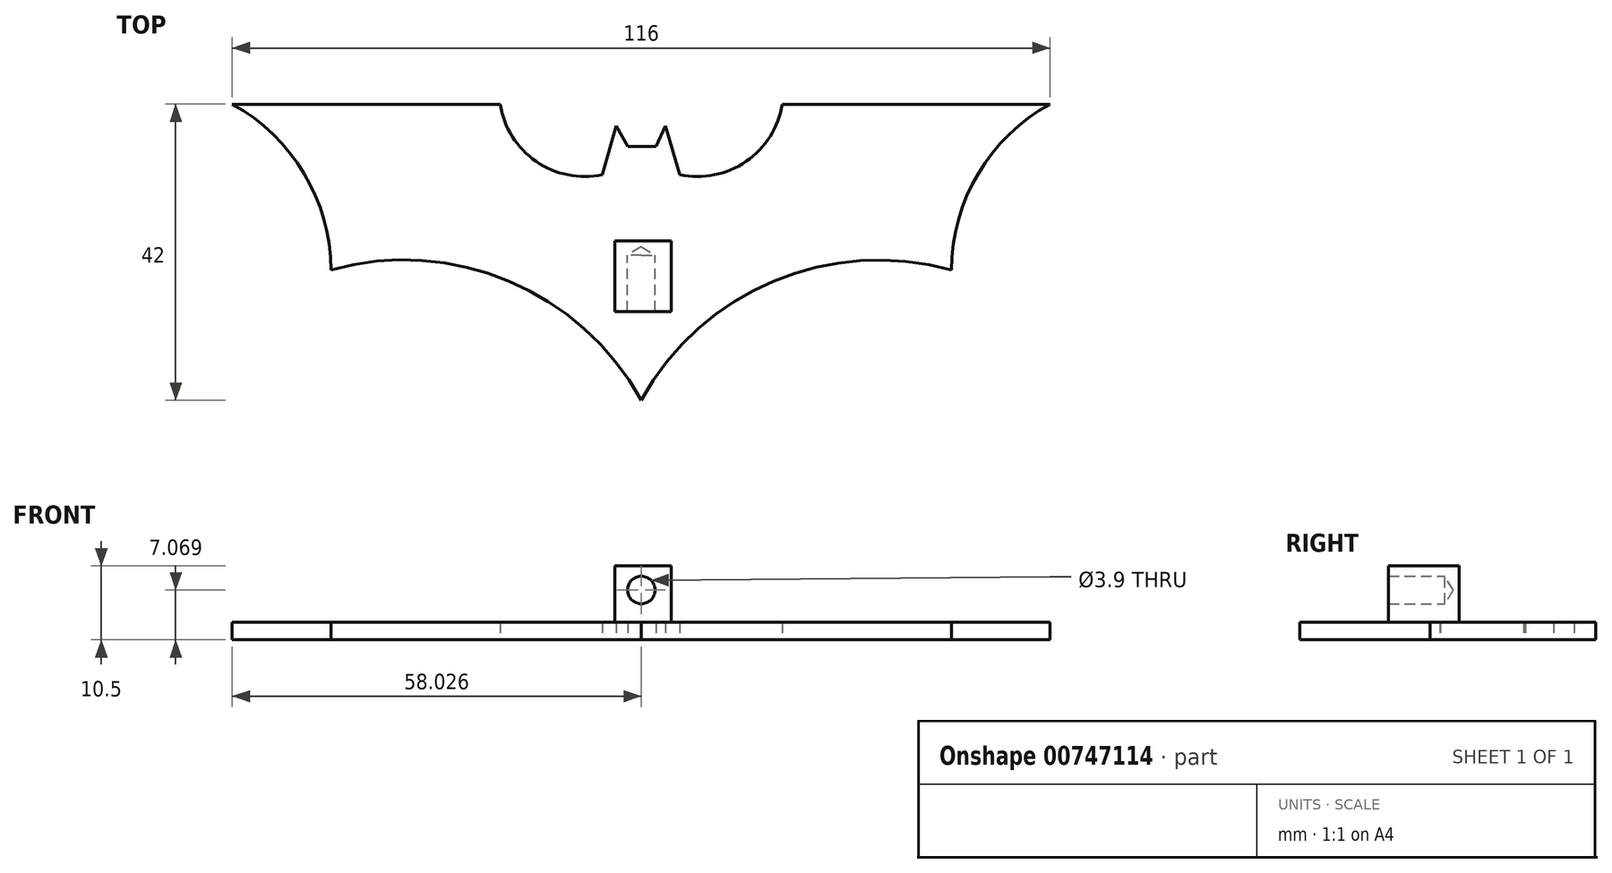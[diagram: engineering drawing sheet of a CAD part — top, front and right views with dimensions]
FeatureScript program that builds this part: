
annotation { "Feature Type Name" : "Feature", "Feature Type Description" : "" }
export const myFeature = defineFeature(function(context is Context, id is Id, definition is map)
    precondition{}
    {
        {
            var Q0;
            Q0=qCreatedBy(makeId("Top.planeOp"),FACE);
            var sketch = newSketch(context, id + "F0", { "sketchPlane" : qUnion([Q0])});
            skLineSegment(sketch, "E0", {"start": v(-58, 14.7) * mm, "end": v(-20, 14.7) * mm});
            skLineSegment(sketch, "E1", {"start": v(20, 14.7) * mm, "end": v(58, 14.7) * mm});
            skLineSegment(sketch, "E2", {"start": v(-5.5, 4.7) * mm, "end": v(-3.54, 11.63) * mm});
            skLineSegment(sketch, "E3", {"start": v(-3.54, 11.63) * mm, "end": v(-1.92, 8.7) * mm});
            skLineSegment(sketch, "E4", {"start": v(-1.92, 8.7) * mm, "end": v(2.08, 8.7) * mm});
            skLineSegment(sketch, "E5", {"start": v(2.08, 8.7) * mm, "end": v(3.46, 11.63) * mm});
            skLineSegment(sketch, "E6", {"start": v(3.46, 11.63) * mm, "end": v(5.5, 4.7) * mm});
            skArc(sketch, "E7", {"start": v(0, -27.3) * mm, "mid": v(-18.78, -10.4) * mm, "end": v(-44, -8.8) * mm});
            skArc(sketch, "E8", {"start": v(44, -8.8) * mm, "mid": v(18.8, -10.43) * mm, "end": v(0, -27.3) * mm});
            skArc(sketch, "E9", {"start": v(5.5, 4.7) * mm, "mid": v(14.9, 6.58) * mm, "end": v(20, 14.7) * mm});
            skArc(sketch, "E10", {"start": v(-20, 14.7) * mm, "mid": v(-14.9, 6.58) * mm, "end": v(-5.5, 4.7) * mm});
            skArc(sketch, "E11", {"start": v(58, 14.7) * mm, "mid": v(47.8, 4.85) * mm, "end": v(44, -8.8) * mm});
            skArc(sketch, "E12", {"start": v(-44, -8.8) * mm, "mid": v(-47.8, 4.85) * mm, "end": v(-58, 14.7) * mm});
            skSolve(sketch);
        }
        {
            var Q0;
            Q0=makeQuery(id+"F0.imprint","IMPRINT",FACE,{"disambiguationData":[TD([[makeQuery(id+"F0.imprint","IMPRINT",EDGE,{"derivedFrom":sQuery(id+"F0.wireOp",EDGE,"E0")}),-1.0]])]});
            extrude(context, id + "F1", {"entities" : qUnion([Q0]), "flatOperationType" : FlatOperationType.REMOVE, "depth" : 2.5 * mm, "offsetDistance" : 25 * mm, "domain" : OperationDomain.MODEL});
        }
        {
            var Q0;
            Q0=makeQuery(id+"F1.opExtrude","CAP_FACE",FACE,{"disambiguationData":[OSD([sQuery(id+"F0.wireOp",EDGE,"E0"),sQuery(id+"F0.wireOp",EDGE,"E1"),sQuery(id+"F0.wireOp",EDGE,"E2"),sQuery(id+"F0.wireOp",EDGE,"E3"),sQuery(id+"F0.wireOp",EDGE,"E4"),sQuery(id+"F0.wireOp",EDGE,"E5"),sQuery(id+"F0.wireOp",EDGE,"E6"),sQuery(id+"F0.wireOp",EDGE,"E7"),sQuery(id+"F0.wireOp",EDGE,"E8"),sQuery(id+"F0.wireOp",EDGE,"E9"),sQuery(id+"F0.wireOp",EDGE,"E10"),sQuery(id+"F0.wireOp",EDGE,"E11"),sQuery(id+"F0.wireOp",EDGE,"E12")])],"isStart":false});
            var sketch = newSketch(context, id + "F2", { "sketchPlane" : qUnion([Q0])});
            skLineSegment(sketch, "E13.bottom", {"start": v(-3.73, -4.71) * mm, "end": v(4.27, -4.71) * mm});
            skLineSegment(sketch, "E13.top", {"start": v(-3.73, -14.71) * mm, "end": v(4.27, -14.71) * mm});
            skLineSegment(sketch, "E13.left", {"start": v(-3.73, -4.71) * mm, "end": v(-3.73, -14.71) * mm});
            skLineSegment(sketch, "E13.right", {"start": v(4.27, -4.71) * mm, "end": v(4.27, -14.71) * mm});
            skSolve(sketch);
        }
        {
            var Q0;
            Q0 = qSketchRegion(id + "F2", true);
            extrude(context, id + "F3", {"entities" : qUnion([Q0]), "operationType" : NewBodyOperationType.ADD, "flatOperationType" : FlatOperationType.REMOVE, "depth" : 8 * mm, "offsetDistance" : 25 * mm, "domain" : OperationDomain.MODEL});
        }
        {
            var Q0;
            Q0=makeQuery(id+"F3.opExtrude","SWEPT_FACE",FACE,{"disambiguationData":[OSD([sQuery(id+"F2.wireOp",EDGE,"E13.top")])]});
            var sketch = newSketch(context, id + "F4", { "sketchPlane" : qUnion([Q0])});
            skCircle(sketch, "E14", {"center": v(0.03, 7.07) * mm, "radius": 1.95 * mm});
            skSolve(sketch);
        }
        {
            var Q0;
            Q0=sQuery(id+"F4.wireOp",VERTEX,"E14.center");
            var Q1;
            Q1=makeQuery(id+"F1.opExtrude","SWEPT_BODY",BODY,{"disambiguationData":[OSD([sQuery(id+"F0.wireOp",EDGE,"E0"),sQuery(id+"F0.wireOp",EDGE,"E1"),sQuery(id+"F0.wireOp",EDGE,"E2"),sQuery(id+"F0.wireOp",EDGE,"E3"),sQuery(id+"F0.wireOp",EDGE,"E4"),sQuery(id+"F0.wireOp",EDGE,"E5"),sQuery(id+"F0.wireOp",EDGE,"E6"),sQuery(id+"F0.wireOp",EDGE,"E7"),sQuery(id+"F0.wireOp",EDGE,"E8"),sQuery(id+"F0.wireOp",EDGE,"E9"),sQuery(id+"F0.wireOp",EDGE,"E10"),sQuery(id+"F0.wireOp",EDGE,"E11"),sQuery(id+"F0.wireOp",EDGE,"E12")])]});
            hole(context, id + "F5", {"style" : HoleStyle.SIMPLE, "endStyle" : HoleEndStyle.BLIND, "holeDiameter" : 3.9 * mm, "majorDiameter" : 5 * mm, "holeDepth" : 8 * mm, "isTappedThrough" : true, "tappedDepth" : 12 * mm, "tapClearance" : 3, "locations" : qUnion([Q0]), "scope" : qUnion([Q1]), "startStyle" : HoleStartStyle.PART});
        }
    });
